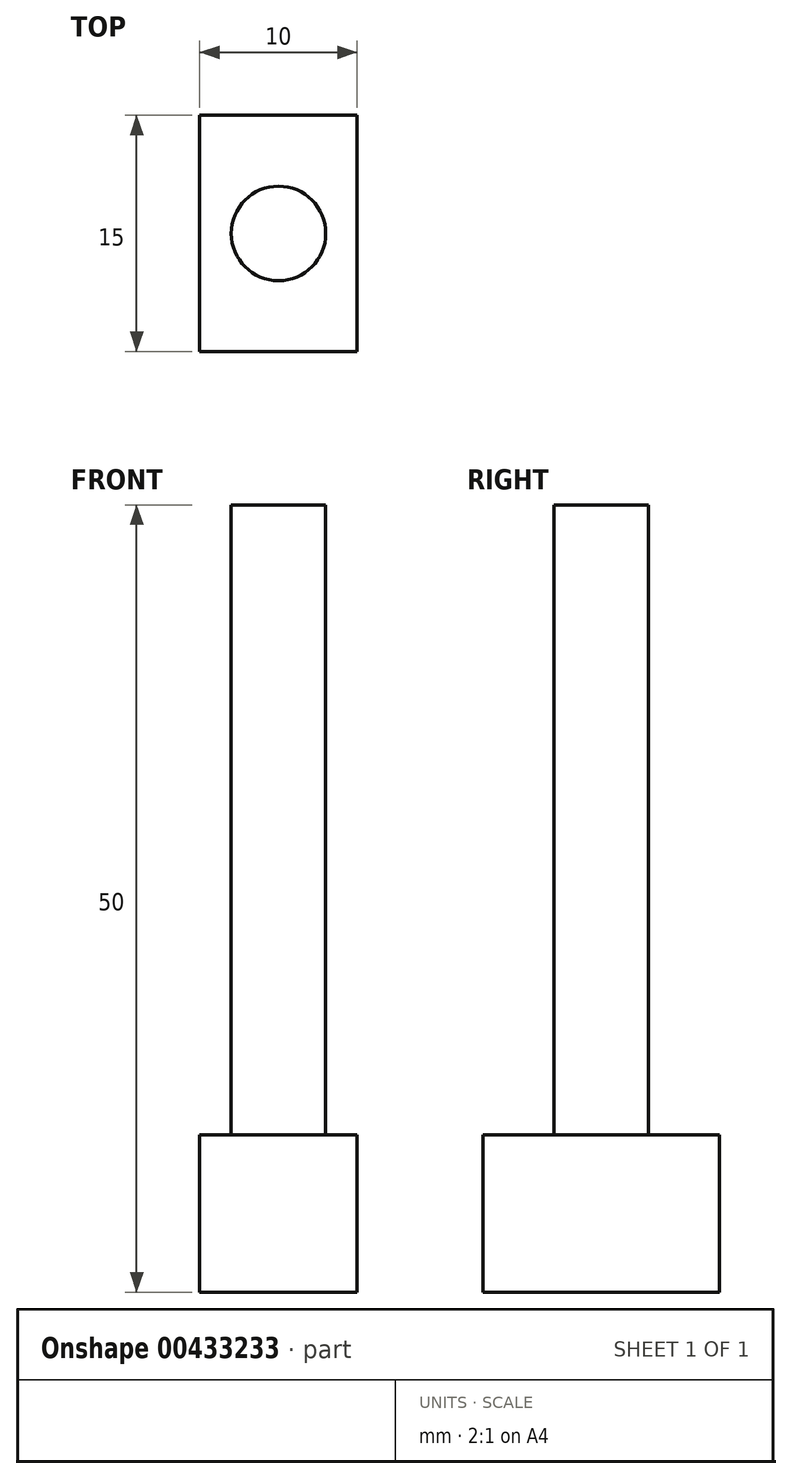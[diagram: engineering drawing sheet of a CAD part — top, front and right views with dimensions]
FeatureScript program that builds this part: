
annotation { "Feature Type Name" : "Feature", "Feature Type Description" : "" }
export const myFeature = defineFeature(function(context is Context, id is Id, definition is map)
    precondition{}
    {
        {
            var Q0;
            Q0=qCreatedBy(makeId("Top.planeOp"),FACE);
            var sketch = newSketch(context, id + "F0", { "sketchPlane" : qUnion([Q0])});
            skLineSegment(sketch, "E0.bottom", {"start": v(-5, 7.5) * mm, "end": v(5, 7.5) * mm});
            skLineSegment(sketch, "E0.top", {"start": v(-5, -7.5) * mm, "end": v(5, -7.5) * mm});
            skLineSegment(sketch, "E0.left", {"start": v(-5, 7.5) * mm, "end": v(-5, -7.5) * mm});
            skLineSegment(sketch, "E0.right", {"start": v(5, 7.5) * mm, "end": v(5, -7.5) * mm});
            skPoint(sketch, "E0.middle", {"position": v(0, 0) * mm});
            skSolve(sketch);
        }
        {
            var Q0;
            Q0 = qSketchRegion(id + "F0", true);
            extrude(context, id + "F1", {"entities" : qUnion([Q0]), "depth" : 10 * mm});
        }
        {
            var Q0;
            Q0=makeQuery(id+"F1.opExtrude","CAP_FACE",FACE,{"disambiguationData":[OSD([sQuery(id+"F0.wireOp",EDGE,"E0.bottom"),sQuery(id+"F0.wireOp",EDGE,"E0.top"),sQuery(id+"F0.wireOp",EDGE,"E0.left"),sQuery(id+"F0.wireOp",EDGE,"E0.right")])],"isStart":false});
            var sketch = newSketch(context, id + "F2", { "sketchPlane" : qUnion([Q0])});
            skLineSegment(sketch, "E1", {"start": v(-5, 0) * mm, "end": v(-3, 0) * mm, "construction": true});
            skCircle(sketch, "E2", {"center": v(0, 0) * mm, "radius": 3 * mm});
            skSolve(sketch);
        }
        {
            var Q0;
            Q0 = qSketchRegion(id + "F2", true);
            extrude(context, id + "F3", {"entities" : qUnion([Q0]), "operationType" : NewBodyOperationType.ADD, "depth" : 40 * mm});
        }
    });
